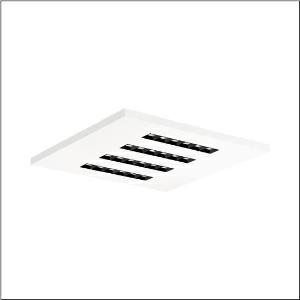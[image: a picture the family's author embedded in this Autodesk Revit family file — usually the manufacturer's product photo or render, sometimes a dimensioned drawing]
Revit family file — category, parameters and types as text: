
# Revit family: silica_r__21_square_51mx6kds34w_2a5b
name_source: partatom
category: Lighting Fixtures
units: mm (PartAtom-declared; Revit-internal decimal feet)

## family parameters
Cut with Voids When Loaded = No
Host = Face
Light Source = No
Part Type = Normal
Room Calculation Point = No
Round Connector Dimension = Use Diameter
Shared = No

## types (1)
- --- (1 x LED, 4600 lm, 31.9 W, 3000K)
    Apparent Load = 32 VA
    CIE Flux Codes = 86 100 100 100 100
    Color Rendering = 80
    Color Temperature = 3000K
    Default Elevation = 1800 mm
    Description = Silica® 21 Square, office luminaire, primary light control with lens, of PMMA, primary anti-glare with reflector, of PC, black, CAT 2 (L<= 3000cd/m²), light emission: direct distribution, primary light characteristic: symmetric, installation type: lay-in mounting, LED, rated luminous flux: 4.600lm, luminous efficacy: 144lm/W, light colour: 830, colour temperature: 3000K, with terminal, 5-pole, mains connection: 220..240V, AC, 50/60Hz, rated input power: 31.9W, luminaire housing, of sheet steel, coated, traffic white (RAL 9016), module: M600, length: 597mm, width: 597mm, height: 33mm, protection rating (complete): IP20, insulation class (complete): insulation class I (protective earthing), certification: CE, permissible operating ambient temperature: -20..+40°C, standard: EN 50419, packaging unit: 1 piece
    Height = 0 mm  [stored 0 ft]
    Lamp = 1 x LED
    Lamp Light Flux = 4600 lm
    Lamp Power = 31.9 W
    Lamp count = 1
    Length = 597 mm
    Luminous efficacy = 144 lm/W
    Manufacturer = Siteco
    ModVariant = No
    Model = 51MX6KDS34W
    Mounting Place = Ceiling
    Mounting Type = Recessed
    Number of Poles = 1
    OnlyDefault = Yes
    Power Factor = 1
    Product Name = Silica® 21 Square
    Product group = office luminaire | ceiling recessed
    ProductGroupID = 400
    Protection Class = Protection class I
    Protection Degree = IP 20
    RLX_Detail_Level = 1
    RLX_Emergency_Light_Flux = 0 lm
    RLX_Emergency_Type = 0
    RLX_Emergency_Type_DB = No
    RlxData = <blob elided: 40305 chars, md5=8743884f>
    Socket = socket
    Standby Power = 0 W
    System Light Flux = 4600 lm
    System Power = 32 W
    Type Comments = factory setting: luminous flux: 100 % | dim-lin: 254 | 430 mA
    Type Image = l_1275207.jpg
    URL = http://relux.com
    VarID = @adj_053439
    Voltage = 0 V
    Weight = 0.00 kg
    Width = 597 mm

note: [stored X ft] marks values corroborated as IEEE doubles in the binary element streams (Revit-internal decimal feet)

## geometry (parser evidence)
native form markers: Blend x4, Sweep x10
no freeform markers — native parametric forms only
